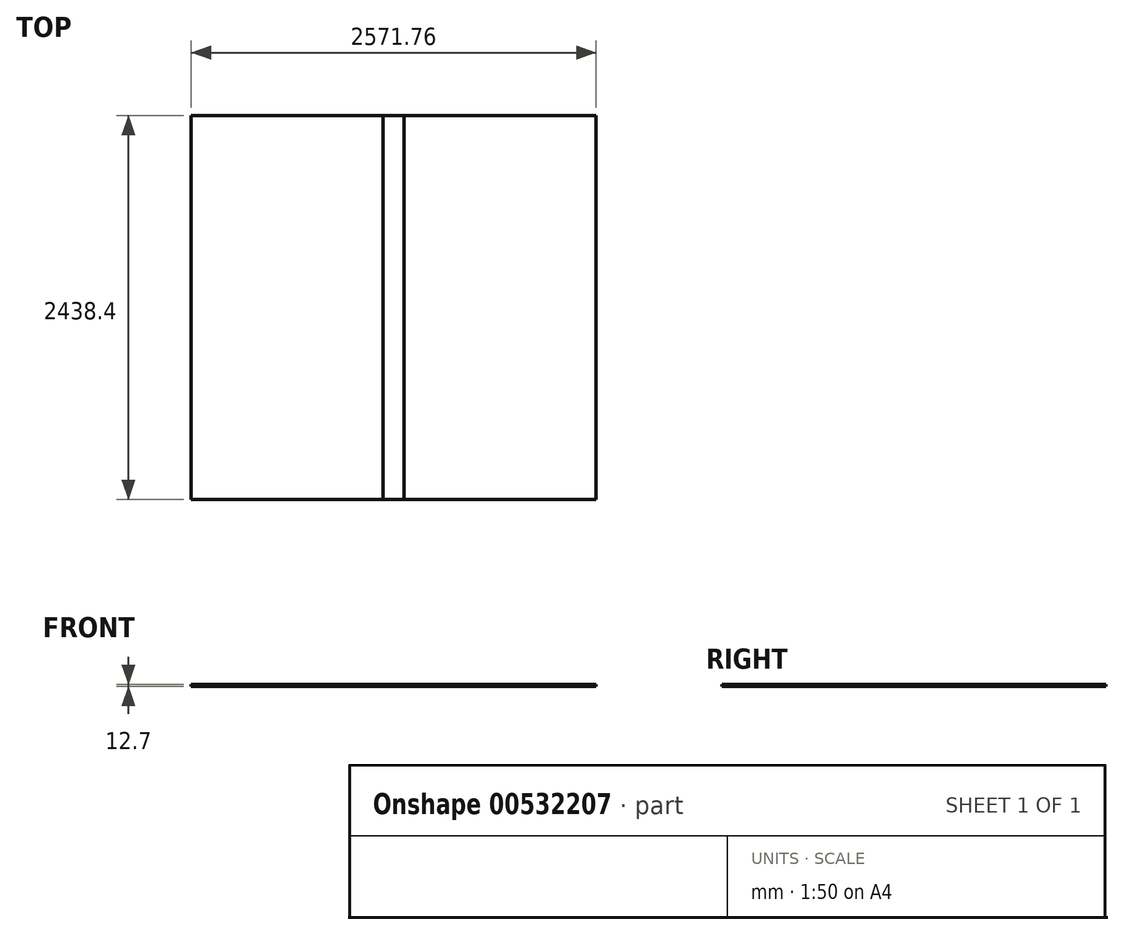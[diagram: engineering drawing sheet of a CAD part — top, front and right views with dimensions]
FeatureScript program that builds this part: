
annotation { "Feature Type Name" : "Feature", "Feature Type Description" : "" }
export const myFeature = defineFeature(function(context is Context, id is Id, definition is map)
    precondition{}
    {
        {
            var Q0;
            Q0=qCreatedBy(makeId("Top.planeOp"),FACE);
            var sketch = newSketch(context, id + "F0", { "sketchPlane" : qUnion([Q0])});
            skLineSegment(sketch, "E0.bottom", {"start": v(1285.87, 1219.2) * mm, "end": v(-1285.88, 1219.2) * mm});
            skLineSegment(sketch, "E0.top", {"start": v(1285.88, -1219.2) * mm, "end": v(-1285.87, -1219.2) * mm});
            skLineSegment(sketch, "E0.left", {"start": v(1285.88, 1219.2) * mm, "end": v(1285.88, -1219.2) * mm});
            skLineSegment(sketch, "E0.right", {"start": v(-1285.88, 1219.2) * mm, "end": v(-1285.87, -1219.2) * mm});
            skPoint(sketch, "E0.middle", {"position": v(0, 0) * mm});
            skLineSegment(sketch, "E1", {"start": v(-66.67, 1219.2) * mm, "end": v(-66.67, -1219.2) * mm});
            skLineSegment(sketch, "E2", {"start": v(66.68, -1219.2) * mm, "end": v(66.67, 1219.2) * mm});
            skSolve(sketch);
        }
        {
            var Q0;
            {var subQ0=sQuery(id+"F0.wireOp",EDGE,"E0.right");Q0=makeQuery(id+"F0.imprint","IMPRINT",FACE,{"disambiguationData":[TD([[makeQuery(id+"F0.imprint","IMPRINT",EDGE,{"derivedFrom":subQ0}),1.0]])]});}
            extrude(context, id + "F1", {"entities" : qUnion([Q0]), "depth" : 12.7 * mm, "offsetDistance" : 25.4 * mm});
        }
        {
            var Q0;
            {var subQ0=sQuery(id+"F0.wireOp",EDGE,"E0.left");Q0=makeQuery(id+"F0.imprint","IMPRINT",FACE,{"disambiguationData":[TD([[makeQuery(id+"F0.imprint","IMPRINT",EDGE,{"derivedFrom":subQ0}),-1.0]])]});}
            extrude(context, id + "F2", {"entities" : qUnion([Q0]), "depth" : 12.7 * mm, "offsetDistance" : 25.4 * mm});
        }
        {
            var Q0;
            {var subQ0=sQuery(id+"F0.wireOp",EDGE,"E1");Q0=makeQuery(id+"F0.imprint","IMPRINT",FACE,{"disambiguationData":[TD([[makeQuery(id+"F0.imprint","IMPRINT",EDGE,{"derivedFrom":subQ0}),1.0]])]});}
            extrude(context, id + "F3", {"entities" : qUnion([Q0]), "depth" : 12.7 * mm, "offsetDistance" : 25.4 * mm});
        }
    });
